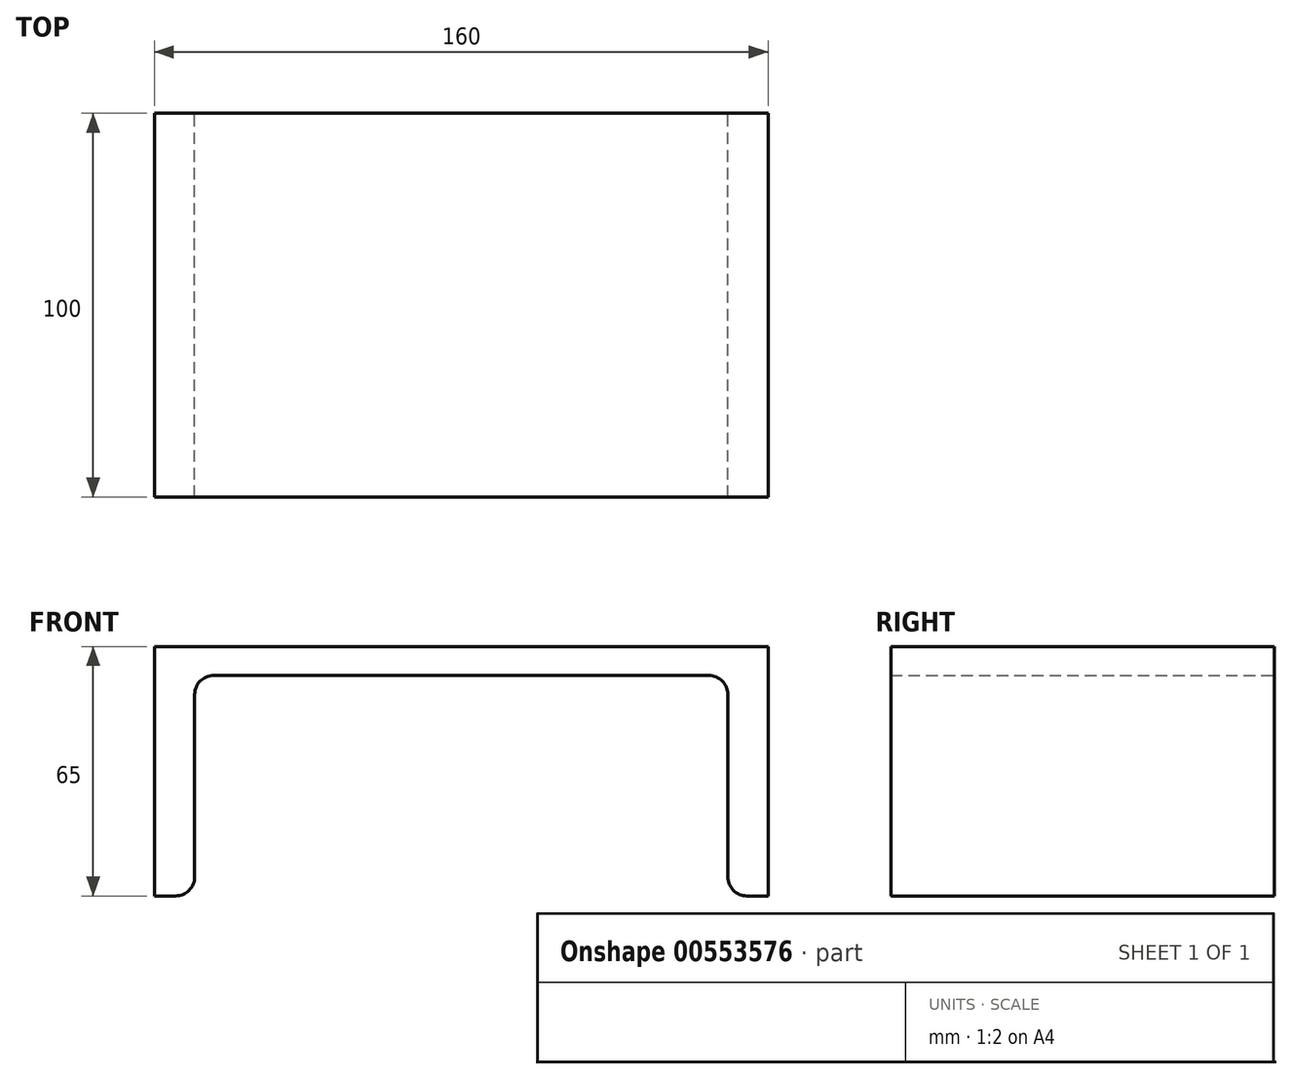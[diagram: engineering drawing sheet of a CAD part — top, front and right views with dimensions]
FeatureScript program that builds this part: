
annotation { "Feature Type Name" : "Feature", "Feature Type Description" : "" }
export const myFeature = defineFeature(function(context is Context, id is Id, definition is map)
    precondition{}
    {
        {
            var Q0;
            Q0=qCreatedBy(makeId("Front.planeOp"),FACE);
            var sketch = newSketch(context, id + "F0", { "sketchPlane" : qUnion([Q0])});
            skLineSegment(sketch, "E0", {"start": v(-28.73, 32.34) * mm, "end": v(131.27, 32.34) * mm});
            skLineSegment(sketch, "E1", {"start": v(131.27, 32.34) * mm, "end": v(131.27, -32.66) * mm});
            skLineSegment(sketch, "E2", {"start": v(-28.73, 32.34) * mm, "end": v(-28.73, -32.66) * mm});
            skLineSegment(sketch, "E3", {"start": v(-13.23, 24.84) * mm, "end": v(115.77, 24.84) * mm});
            skLineSegment(sketch, "E4", {"start": v(-18.23, 19.84) * mm, "end": v(-18.23, -27.66) * mm});
            skLineSegment(sketch, "E5", {"start": v(120.77, 19.84) * mm, "end": v(120.77, -27.66) * mm});
            skPoint(sketch, "E6.visualSharp", {"position": v(-18.23, 24.84) * mm});
            skArc(sketch, "E6.filletArc", {"start": v(-13.23, 24.84) * mm, "mid": v(-16.76, 23.38) * mm, "end": v(-18.23, 19.84) * mm});
            skPoint(sketch, "E7.visualSharp", {"position": v(120.77, 24.84) * mm});
            skArc(sketch, "E7.filletArc", {"start": v(120.77, 19.84) * mm, "mid": v(119.3, 23.38) * mm, "end": v(115.77, 24.84) * mm});
            skLineSegment(sketch, "E8", {"start": v(131.27, -32.66) * mm, "end": v(125.77, -32.66) * mm});
            skPoint(sketch, "E9.visualSharp", {"position": v(120.77, -32.66) * mm});
            skArc(sketch, "E9.filletArc", {"start": v(120.77, -27.66) * mm, "mid": v(122.24, -31.2) * mm, "end": v(125.77, -32.66) * mm});
            skLineSegment(sketch, "E10", {"start": v(-28.73, -32.66) * mm, "end": v(-23.23, -32.66) * mm});
            skPoint(sketch, "E11.visualSharp", {"position": v(-18.23, -32.66) * mm});
            skArc(sketch, "E11.filletArc", {"start": v(-23.23, -32.66) * mm, "mid": v(-19.7, -31.2) * mm, "end": v(-18.23, -27.66) * mm});
            skSolve(sketch);
        }
        {
            var Q0;
            Q0 = qSketchRegion(id + "F0", true);
            extrude(context, id + "F1", {"entities" : qUnion([Q0]), "depth" : 100 * mm, "offsetDistance" : 25 * mm});
        }
    });
